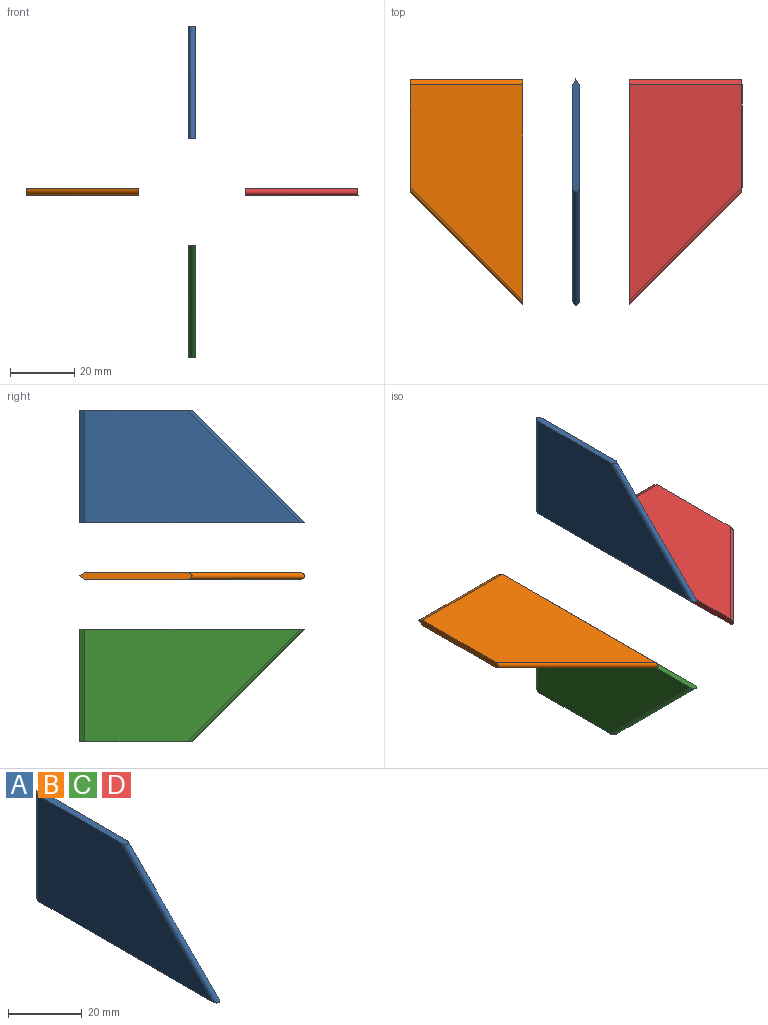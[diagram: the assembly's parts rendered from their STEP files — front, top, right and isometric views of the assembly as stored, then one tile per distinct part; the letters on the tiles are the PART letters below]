
ASSEMBLY  parts=4 mates=3
PART A: 7 faces, bbox 2x70x36.4 mm
  f0: plane 66.88x35.03mm, normal (1,0,0), area 1729.4mm2, adj f2,f3,f4,f5
  f1: plane 66.88x35.03mm, normal (-1,0,0), area 1729.4mm2, adj f2,f3,f4,f6
  f2: cylinder r=1mm len=36.41mm, axis (0,0.71,0.71), area 155.6mm2, adj f0,f1,f3,f4
  f3: plane 35x2mm, normal (0,0,1), area 67.7mm2, adj f0,f1,f2,f5,f6
  f4: cylinder r=16.5mm len=70mm, axis (0,1,0), area 137.8mm2, adj f0,f1,f2,f5,f6
  f5: plane 35.03x1.73mm, normal (0.87,0.5,0), area 70mm2, adj f0,f3,f4,f6
  f6: plane 35.03x1.73mm, normal (-0.87,0.5,0), area 70mm2, adj f1,f3,f4,f5
PART B: same geometry as A
PART C: same geometry as A
PART D: same geometry as A
PLACE A t=(-30.35,26.98,-3.19)mm fixed
PLACE B rot(axis=(0,-1,0),90deg) t=(-46.85,26.98,-19.69)mm
PLACE C rot(axis=(0,-1,0),180deg) t=(-30.35,26.98,-36.19)mm
PLACE D rot(axis=(0,1,0),90deg) t=(-13.85,26.98,-19.69)mm
MATE revolute A.f4 <-> B.f4  axis (0,1,0) through (-30.35,-8.03,-19.69)mm
MATE revolute A.f4 <-> C.f4  axis (0,1,0) through (-30.35,-8.03,-19.69)mm
MATE revolute A.f4 <-> D.f4  axis (0,1,0) through (-30.35,-8.03,-19.69)mm
